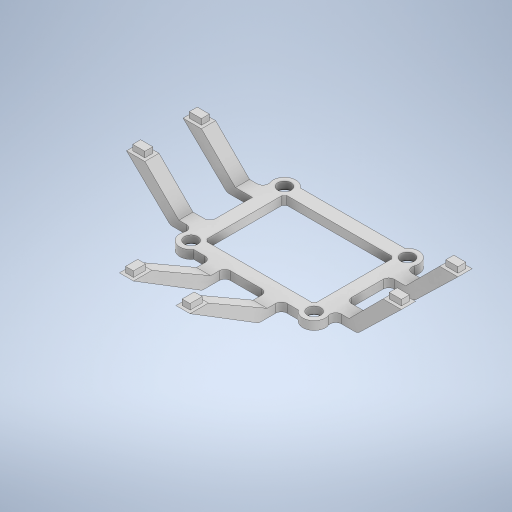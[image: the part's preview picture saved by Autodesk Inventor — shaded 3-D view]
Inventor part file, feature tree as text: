
AUTODESK INVENTOR PART (.ipt)
format: ipt  version: 2024.2 (Build 282272000, 272)  size: 466,944 bytes
history: native  units: mm
features: extrude x5, mirror x5, sketch x5, plane x4, fillet x2, chamfer x1
ambient origin geometry x8: Origin, YZ Plane, XZ Plane, XY Plane, X Axis, Y Axis, Z Axis, Center Point
bodies: Solid1 (feature_tree)
feature tree (22):
  extrude  "Extrusion1"  Depth=8.0mm
  chamfer  "Chamfer1"  Distance=4.7mm
  plane  "Work Plane2"
  extrude  "Extrusion2"  Depth=8.0mm
  plane  "Work Plane4"
  plane  "Work Plane5"
  mirror  "Mirror1"
  mirror  "Mirror2"
  plane  "Work Plane6"
  extrude  "Extrusion5"  Depth=4.0mm
  mirror  "Mirror5"
  extrude  "Extrusion4"  Depth=4.0mm
  mirror  "Mirror3"
  mirror  "Mirror4"
  extrude  "Extrusion6"  Depth=4.0mm
  fillet  "Fillet1"  Radius=4.0mm
  fillet  "Fillet2"  Radius=4.0mm
  sketch  "Sketch1"  dims[d0=4.7mm d1=8.0mm]
  sketch  "Sketch2"  dims[d2=4.7mm]
  sketch  "Sketch5"  dims[d3=8.0mm]
  sketch  "Sketch7"  dims[d4=4.7mm]
  sketch  "Sketch8"  dims[d5=8.0mm d6=4.7mm d7=8.0mm d8=4.0mm d9=4.0mm d10=4.0mm d11=4.0mm d12=4.0mm d13=4.0mm d14=4.0mm d15=4.0mm d16=33.0mm d17=4.7mm d18=4.7mm d19=4.7mm d20=4.7mm d21=2.35mm d22=2.35mm d23=2.35mm d24=2.35mm d25=43.5mm d26=3.0mm d27=0.0mm d28=0.5mm d29=2.0mm d30=45.0deg d32=4.0mm d41=5.0mm d42=0.0mm d47=21.75mm d48=16.5mm d49=6.5mm d61=9.0mm d62=4.3mm d63=2.8mm d64=1.1mm d65=1.1mm d66=2.0mm d67=0.0mm d71=9.25mm d72=8.0mm d73=6.5mm d76=5.0mm d77=0.0mm d78=2.8mm d79=4.3mm d80=2.8mm d81=4.3mm d82=1.1mm d83=1.1mm d84=1.1mm d85=1.1mm d86=2.0mm d87=0.0mm d91=6.0mm d93=45.0deg d94=15.0mm d95=15.0mm d96=2.0mm d97=2.0mm d98=5.0mm d99=30.0deg]
